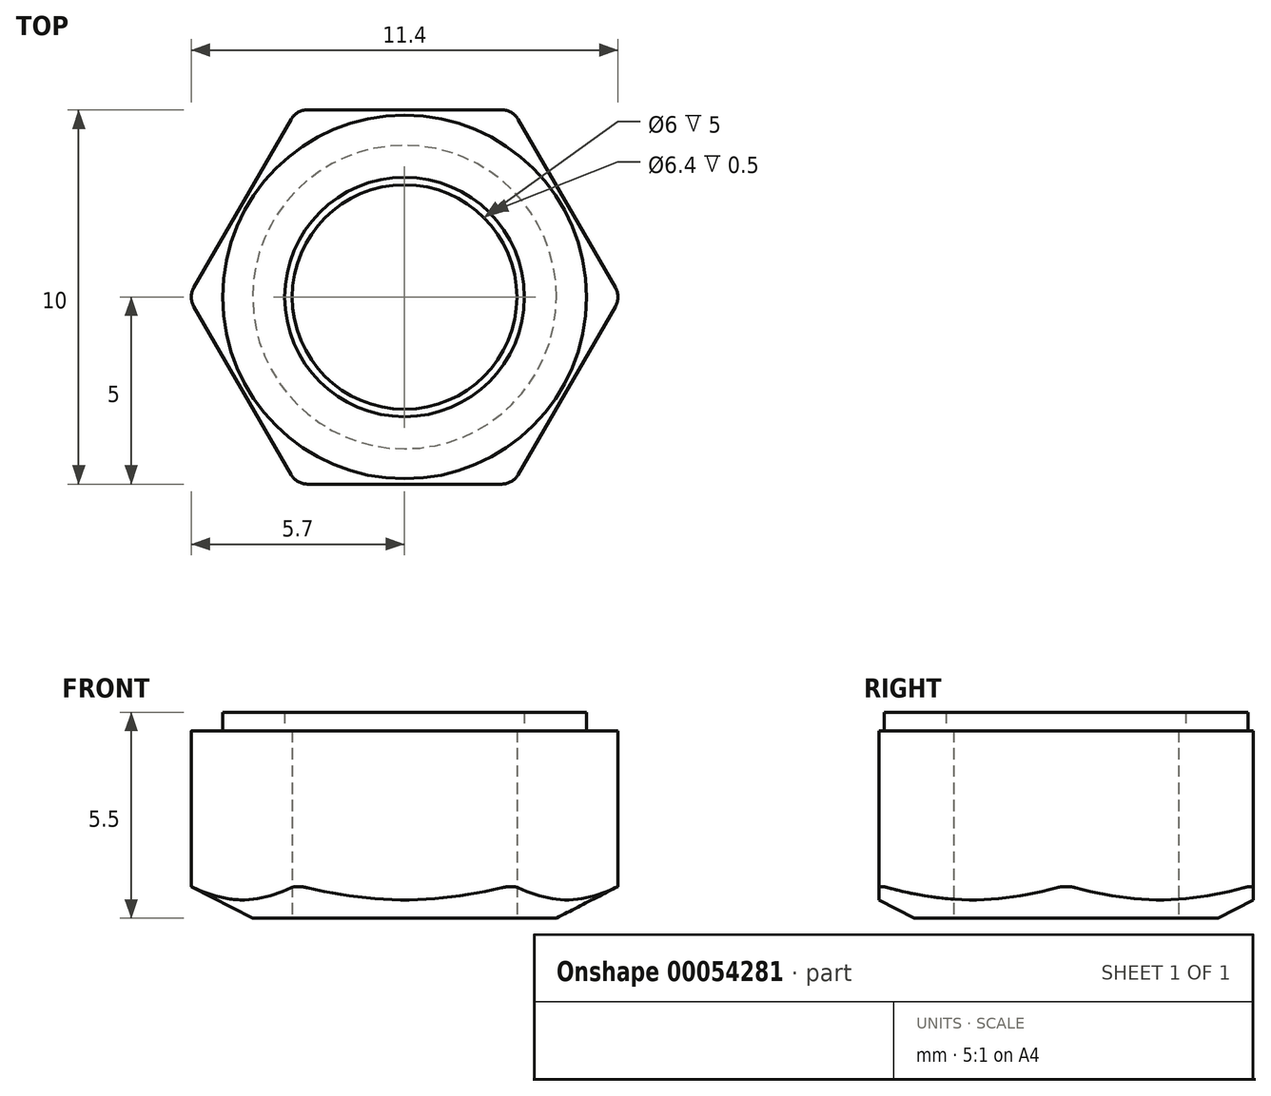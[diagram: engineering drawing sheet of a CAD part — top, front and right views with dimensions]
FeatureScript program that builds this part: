
annotation { "Feature Type Name" : "Feature", "Feature Type Description" : "" }
export const myFeature = defineFeature(function(context is Context, id is Id, definition is map)
    precondition{}
    {
        {
            var Q0;
            Q0=qCreatedBy(makeId("Top.planeOp"),FACE);
            var sketch = newSketch(context, id + "F0", { "sketchPlane" : qUnion([Q0])});
            skCircle(sketch, "E0.cCircle", {"center": v(0, 0) * mm, "radius": 36.68 * mm, "construction": true});
            skLineSegment(sketch, "E0.0", {"start": v(-36.5, 15.62) * mm, "end": v(-14.77, 36.86) * mm});
            skLineSegment(sketch, "E0.1", {"start": v(-14.77, 36.86) * mm, "end": v(15.62, 36.5) * mm});
            skLineSegment(sketch, "E0.2", {"start": v(15.62, 36.5) * mm, "end": v(36.86, 14.77) * mm});
            skLineSegment(sketch, "E0.3", {"start": v(36.86, 14.77) * mm, "end": v(36.5, -15.62) * mm});
            skLineSegment(sketch, "E0.4", {"start": v(36.5, -15.62) * mm, "end": v(14.77, -36.86) * mm});
            skLineSegment(sketch, "E0.5", {"start": v(14.77, -36.86) * mm, "end": v(-15.62, -36.5) * mm});
            skLineSegment(sketch, "E0.6", {"start": v(-15.62, -36.5) * mm, "end": v(-36.86, -14.77) * mm});
            skLineSegment(sketch, "E0.7", {"start": v(-36.86, -14.77) * mm, "end": v(-36.5, 15.62) * mm});
            skPoint(sketch, "E0.0.midPoint", {"position": v(-25.64, 26.24) * mm});
            skCircle(sketch, "E1.cCircle", {"center": v(0, 0) * mm, "radius": 5 * mm, "construction": true});
            skLineSegment(sketch, "E1.0", {"start": v(-5.77, 0) * mm, "end": v(-2.89, 5) * mm});
            skLineSegment(sketch, "E1.1", {"start": v(-2.89, 5) * mm, "end": v(2.89, 5) * mm});
            skLineSegment(sketch, "E1.2", {"start": v(2.89, 5) * mm, "end": v(5.77, 0) * mm});
            skLineSegment(sketch, "E1.3", {"start": v(5.77, 0) * mm, "end": v(2.89, -5) * mm});
            skLineSegment(sketch, "E1.4", {"start": v(2.89, -5) * mm, "end": v(-2.89, -5) * mm});
            skLineSegment(sketch, "E1.5", {"start": v(-2.89, -5) * mm, "end": v(-5.77, 0) * mm});
            skPoint(sketch, "E1.0.midPoint", {"position": v(-4.33, 2.5) * mm});
            skSolve(sketch);
        }
        {
            var Q0;
            Q0=makeQuery(id+"F0.imprint","IMPRINT",FACE,{"disambiguationData":[TD([[makeQuery(id+"F0.imprint","IMPRINT",EDGE,{"derivedFrom":sQuery(id+"F0.wireOp",EDGE,"E1.0")}),-1.0]])]});
            extrude(context, id + "F1", {"entities" : qUnion([Q0]), "depth" : 5 * mm});
        }
        {
            var Q0;
            Q0=qCreatedBy(makeId("Front.planeOp"),FACE);
            var sketch = newSketch(context, id + "F2", { "sketchPlane" : qUnion([Q0])});
            skLineSegment(sketch, "E2", {"start": v(3.5, -0.29) * mm, "end": v(6, 1) * mm});
            skLineSegment(sketch, "E3", {"start": v(6, 1) * mm, "end": v(6, -0.29) * mm});
            skLineSegment(sketch, "E4", {"start": v(6, -0.29) * mm, "end": v(3.5, -0.29) * mm});
            skLineSegment(sketch, "E5", {"start": v(0, -3.5) * mm, "end": v(0, 7.02) * mm});
            skSolve(sketch);
        }
        {
            var Q0;
            Q0=makeQuery(id+"F2.imprint","IMPRINT",FACE,{"disambiguationData":[TD([[makeQuery(id+"F2.imprint","IMPRINT",EDGE,{"derivedFrom":sQuery(id+"F2.wireOp",EDGE,"E2")}),-1.0]])]});
            var Q1;
            Q1=sQuery(id+"F2.wireOp",EDGE,"E5");
            revolve(context, id + "F3", {"operationType" : NewBodyOperationType.REMOVE, "entities" : qUnion([Q0]), "axis" : qUnion([Q1]), "revolveType" : RevolveType.FULL, "oppositeDirection" : true});
        }
        {
            var Q0;
            Q0=makeQuery(id+"F1.opExtrude","CAP_FACE",FACE,{"disambiguationData":[OSD([sQuery(id+"F0.wireOp",EDGE,"E1.0"),sQuery(id+"F0.wireOp",EDGE,"E1.1"),sQuery(id+"F0.wireOp",EDGE,"E1.2"),sQuery(id+"F0.wireOp",EDGE,"E1.3"),sQuery(id+"F0.wireOp",EDGE,"E1.4"),sQuery(id+"F0.wireOp",EDGE,"E1.5")])],"isStart":true});
            var sketch = newSketch(context, id + "F4", { "sketchPlane" : qUnion([Q0])});
            skCircle(sketch, "E6", {"center": v(0, 0) * mm, "radius": 3 * mm});
            skSolve(sketch);
        }
        {
            var Q0;
            Q0=makeQuery(id+"F4.imprint","IMPRINT",FACE,{"disambiguationData":[TD([[makeQuery(id+"F4.imprint","IMPRINT",EDGE,{"derivedFrom":sQuery(id+"F4.wireOp",EDGE,"E6")}),1.0]])]});
            extrude(context, id + "F5", {"entities" : qUnion([Q0]), "operationType" : NewBodyOperationType.REMOVE, "endBound" : BoundingType.THROUGH_ALL, "oppositeDirection" : true, "depth" : 25 * mm});
        }
        {
            var Q0;
            Q0=makeQuery(id+"F1.opExtrude","SWEPT_EDGE",EDGE,{"disambiguationData":[OSD([sQuery(id+"F0.wireOp",EDGE,"E1.0"),sQuery(id+"F0.wireOp",EDGE,"E1.1")])]});
            fillet(context, id + "F6", {"entities" : qUnion([Q0]), "radius" : .5 * mm, "tangentPropagation" : true, "allowEdgeOverflow" : false});
        }
        {
            var Q0;
            Q0=makeQuery(id+"F1.opExtrude","SWEPT_EDGE",EDGE,{"disambiguationData":[OSD([sQuery(id+"F0.wireOp",EDGE,"E1.0"),sQuery(id+"F0.wireOp",EDGE,"E1.5")])]});
            var Q1;
            Q1=makeQuery(id+"F1.opExtrude","SWEPT_EDGE",EDGE,{"disambiguationData":[OSD([sQuery(id+"F0.wireOp",EDGE,"E1.4"),sQuery(id+"F0.wireOp",EDGE,"E1.5")])]});
            var Q2;
            Q2=makeQuery(id+"F1.opExtrude","SWEPT_EDGE",EDGE,{"disambiguationData":[OSD([sQuery(id+"F0.wireOp",EDGE,"E1.3"),sQuery(id+"F0.wireOp",EDGE,"E1.4")])]});
            var Q3;
            Q3=makeQuery(id+"F1.opExtrude","SWEPT_EDGE",EDGE,{"disambiguationData":[OSD([sQuery(id+"F0.wireOp",EDGE,"E1.2"),sQuery(id+"F0.wireOp",EDGE,"E1.3")])]});
            var Q4;
            Q4=makeQuery(id+"F1.opExtrude","SWEPT_EDGE",EDGE,{"disambiguationData":[OSD([sQuery(id+"F0.wireOp",EDGE,"E1.1"),sQuery(id+"F0.wireOp",EDGE,"E1.2")])]});
            fillet(context, id + "F7", {"entities" : qUnion([Q0, Q1, Q2, Q3, Q4]), "radius" : .5 * mm, "tangentPropagation" : true, "allowEdgeOverflow" : false});
        }
        {
            var Q0;
            Q0=makeQuery(id+"F1.opExtrude","CAP_FACE",FACE,{"disambiguationData":[OSD([sQuery(id+"F0.wireOp",EDGE,"E1.0"),sQuery(id+"F0.wireOp",EDGE,"E1.1"),sQuery(id+"F0.wireOp",EDGE,"E1.2"),sQuery(id+"F0.wireOp",EDGE,"E1.3"),sQuery(id+"F0.wireOp",EDGE,"E1.4"),sQuery(id+"F0.wireOp",EDGE,"E1.5")])],"isStart":false});
            var sketch = newSketch(context, id + "F8", { "sketchPlane" : qUnion([Q0])});
            skSolve(sketch);
        }
        {
            var Q0;
            {var subQ3=sQuery(id+"F0.wireOp",EDGE,"E1.2");Q0=makeQuery(id+"F8.imprint","IMPRINT",FACE,{"disambiguationData":[TD([[makeQuery(id+"F8.imprint","IMPRINT",EDGE,{"derivedFrom":makeQuery(id+"F1.opExtrude","CAP_EDGE",EDGE,{"disambiguationData":[OSD([subQ3])],"isStart":false})}),-1.0]])]});}
            var sketch = newSketch(context, id + "F9", { "sketchPlane" : qUnion([Q0])});
            skCircle(sketch, "E7", {"center": v(0, 0) * mm, "radius": 4.86 * mm});
            skCircle(sketch, "E8", {"center": v(0, 0) * mm, "radius": 3.2 * mm});
            skSolve(sketch);
        }
        {
            var Q0;
            Q0 = qSketchRegion(id + "F9", true);
            extrude(context, id + "F10", {"entities" : qUnion([Q0]), "operationType" : NewBodyOperationType.ADD, "depth" : .5 * mm});
        }
    });
